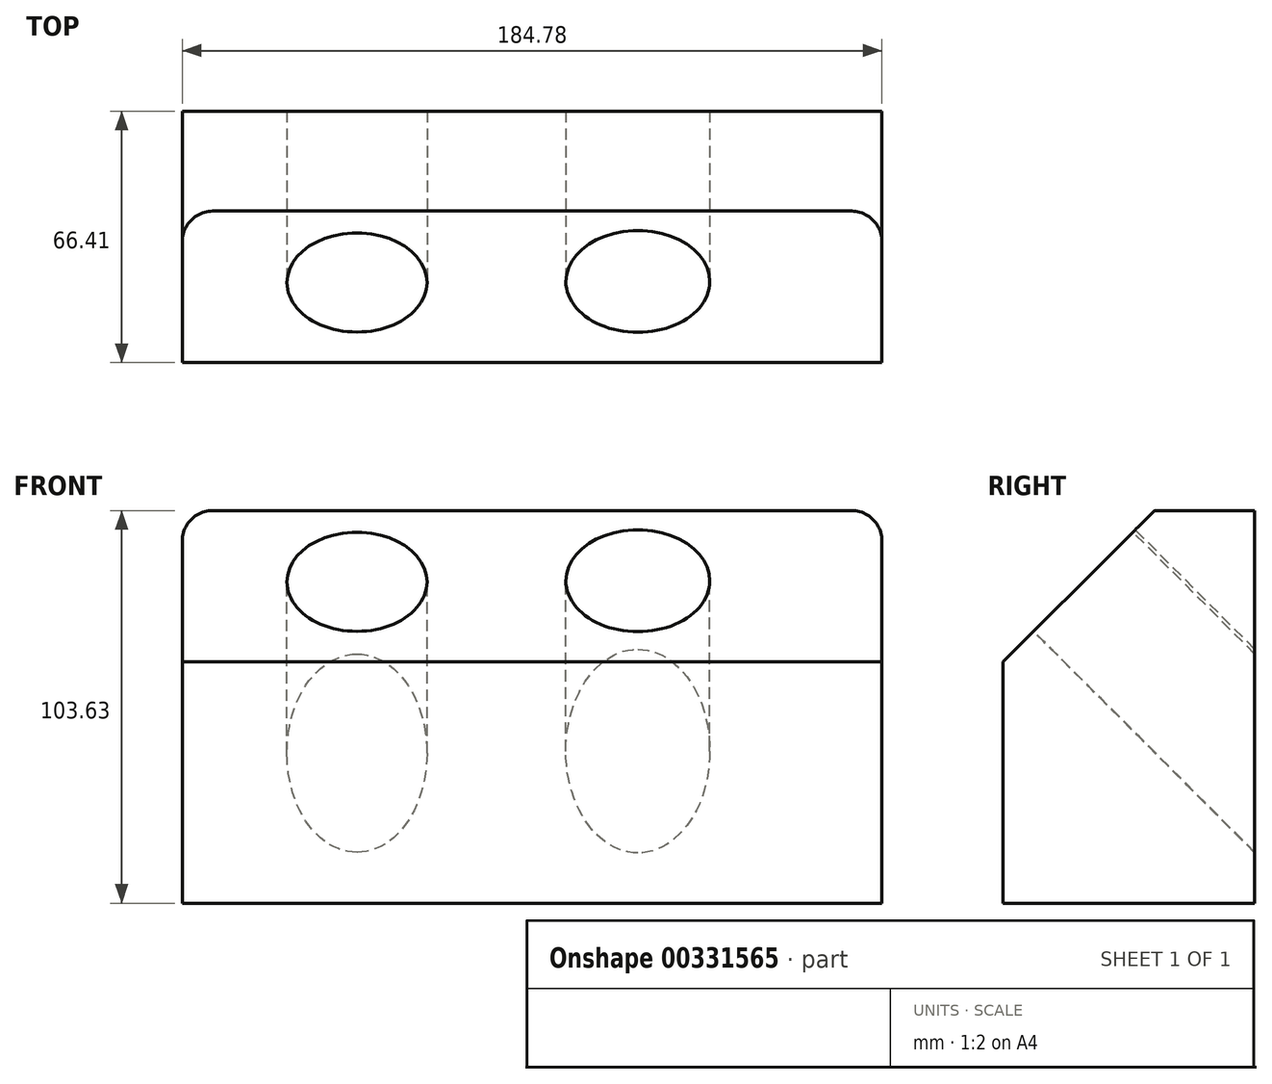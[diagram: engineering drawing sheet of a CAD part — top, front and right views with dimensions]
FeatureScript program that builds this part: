
annotation { "Feature Type Name" : "Feature", "Feature Type Description" : "" }
export const myFeature = defineFeature(function(context is Context, id is Id, definition is map)
    precondition{}
    {
        {
            var Q0;
            Q0=qCreatedBy(makeId("Top.planeOp"),FACE);
            var sketch = newSketch(context, id + "F0", { "sketchPlane" : qUnion([Q0])});
            skLineSegment(sketch, "E0.bottom", {"start": v(-132.47, 66.41) * mm, "end": v(52.3, 66.41) * mm});
            skLineSegment(sketch, "E0.top", {"start": v(-132.47, 0) * mm, "end": v(52.3, 0) * mm});
            skLineSegment(sketch, "E0.left", {"start": v(-132.47, 66.41) * mm, "end": v(-132.47, 0) * mm});
            skLineSegment(sketch, "E0.right", {"start": v(52.3, 66.41) * mm, "end": v(52.3, 0) * mm});
            skSolve(sketch);
        }
        {
            var Q0;
            Q0=makeQuery(id+"F0.imprint","IMPRINT",FACE,{"disambiguationData":[TD([[makeQuery(id+"F0.imprint","IMPRINT",EDGE,{"derivedFrom":sQuery(id+"F0.wireOp",EDGE,"E0.bottom")}),-1.0]])]});
            extrude(context, id + "F1", {"entities" : qUnion([Q0]), "depth" : 103.63 * mm});
        }
        {
            var Q0;
            Q0=makeQuery(id+"F1.opExtrude","CAP_EDGE",EDGE,{"disambiguationData":[OSD([sQuery(id+"F0.wireOp",EDGE,"E0.top")])],"isStart":false});
            chamfer(context, id + "F2", {"entities" : qUnion([Q0]), "width" : 40 * mm, "tangentPropagation" : true});
        }
        {
            var Q0;
            Q0=makeQuery(id+"F2.opChamfer","BLEND_FACE",FACE,{"disambiguationData":[OSD([sQuery(id+"F0.wireOp",EDGE,"E0.top")])]});
            var sketch = newSketch(context, id + "F3", { "sketchPlane" : qUnion([Q0])});
            skCircle(sketch, "E1", {"center": v(-86.33, 74.95) * mm, "radius": 18.31 * mm});
            skSolve(sketch);
        }
        {
            var Q0;
            Q0=makeQuery(id+"F3.imprint","IMPRINT",FACE,{"disambiguationData":[TD([[makeQuery(id+"F3.imprint","IMPRINT",EDGE,{"derivedFrom":sQuery(id+"F3.wireOp",EDGE,"E1")}),-1.0]])]});
            var sketch = newSketch(context, id + "F4", { "sketchPlane" : qUnion([Q0])});
            skCircle(sketch, "E2", {"center": v(-12.18, 75.33) * mm, "radius": 19.2 * mm});
            skSolve(sketch);
        }
        {
            var Q0;
            Q0=sQuery(id+"F3.wireOp",VERTEX,"E1.center");
            var Q1;
            Q1=makeQuery(id+"F1.opExtrude","SWEPT_BODY",BODY,{"disambiguationData":[OSD([sQuery(id+"F0.wireOp",EDGE,"E0.bottom"),sQuery(id+"F0.wireOp",EDGE,"E0.top"),sQuery(id+"F0.wireOp",EDGE,"E0.left"),sQuery(id+"F0.wireOp",EDGE,"E0.right")])]});
            hole(context, id + "F5", {"style" : HoleStyle.SIMPLE, "endStyle" : HoleEndStyle.THROUGH, "holeDiameter" : 37 * mm, "isTappedThrough" : true, "tappedDepth" : 12.7 * mm, "tapClearance" : 3, "locations" : qUnion([Q0]), "scope" : qUnion([Q1])});
        }
        {
            var Q0;
            Q0=sQuery(id+"F4.wireOp",VERTEX,"E2.center");
            var Q1;
            Q1=makeQuery(id+"F1.opExtrude","SWEPT_BODY",BODY,{"disambiguationData":[OSD([sQuery(id+"F0.wireOp",EDGE,"E0.bottom"),sQuery(id+"F0.wireOp",EDGE,"E0.top"),sQuery(id+"F0.wireOp",EDGE,"E0.left"),sQuery(id+"F0.wireOp",EDGE,"E0.right")])]});
            hole(context, id + "F6", {"style" : HoleStyle.SIMPLE, "endStyle" : HoleEndStyle.THROUGH, "holeDiameter" : 38 * mm, "isTappedThrough" : true, "tappedDepth" : 12.7 * mm, "tapClearance" : 3, "locations" : qUnion([Q0]), "scope" : qUnion([Q1])});
        }
        {
            var Q0;
            Q0=makeQuery(id+"F1.opExtrude","CAP_EDGE",EDGE,{"disambiguationData":[OSD([sQuery(id+"F0.wireOp",EDGE,"E0.right")])],"isStart":false});
            fillet(context, id + "F7", {"entities" : qUnion([Q0]), "radius" : 8 * mm, "tangentPropagation" : true, "allowEdgeOverflow" : false});
        }
        {
            var Q0;
            Q0=makeQuery(id+"F1.opExtrude","CAP_EDGE",EDGE,{"disambiguationData":[OSD([sQuery(id+"F0.wireOp",EDGE,"E0.left")])],"isStart":false});
            fillet(context, id + "F8", {"entities" : qUnion([Q0]), "radius" : 8 * mm, "tangentPropagation" : true, "allowEdgeOverflow" : false});
        }
    });
